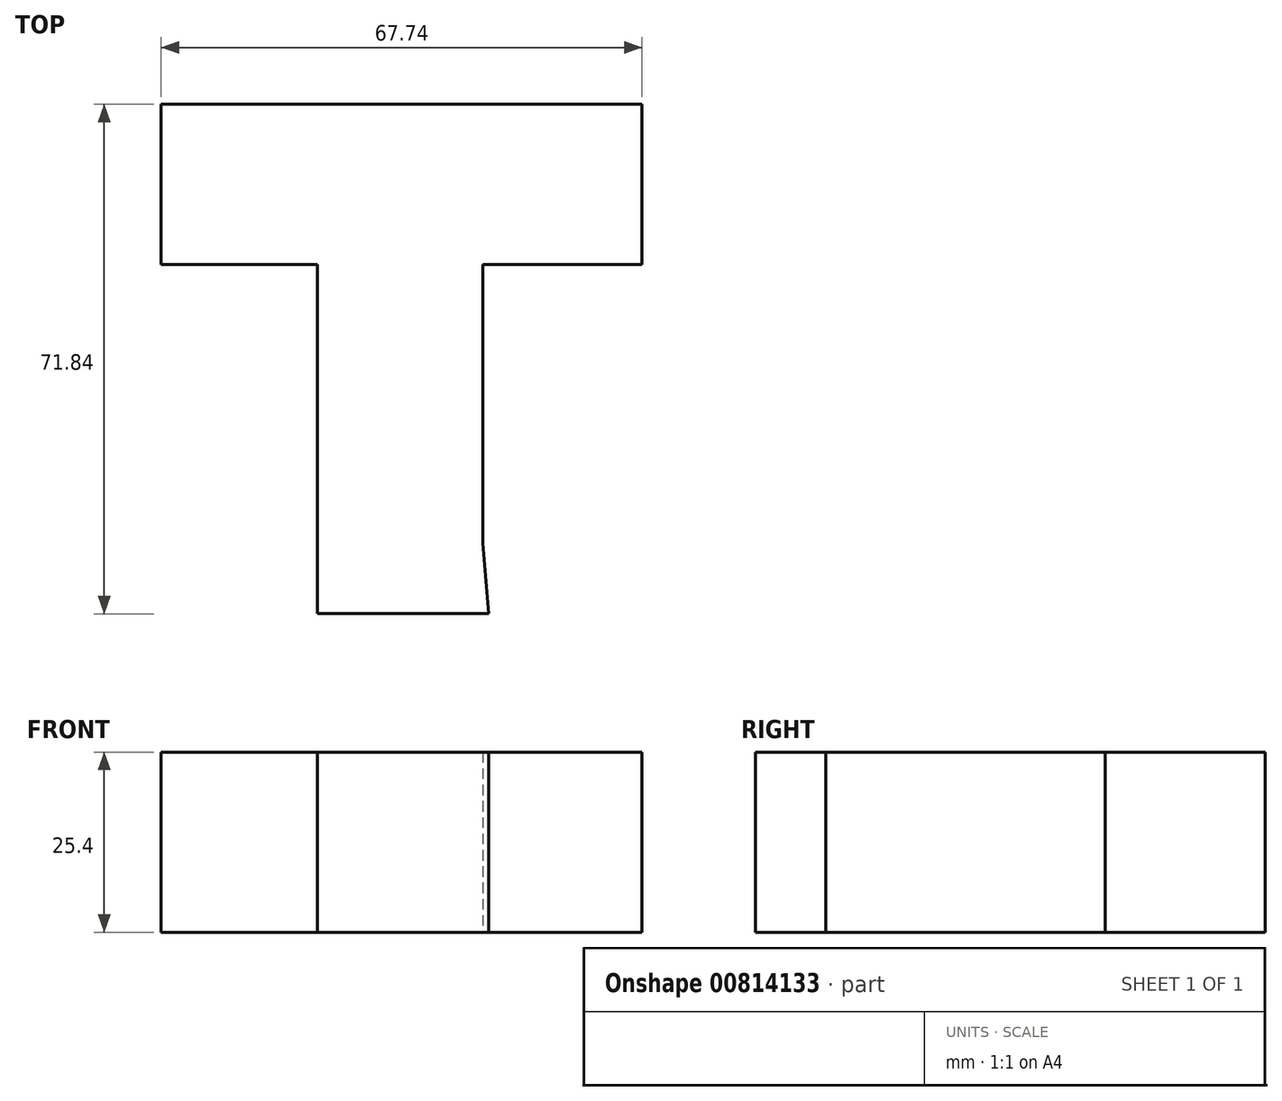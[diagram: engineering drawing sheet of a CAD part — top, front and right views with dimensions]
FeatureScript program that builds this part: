
annotation { "Feature Type Name" : "Feature", "Feature Type Description" : "" }
export const myFeature = defineFeature(function(context is Context, id is Id, definition is map)
    precondition{}
    {
        {
            var Q0;
            Q0=qCreatedBy(makeId("Top.planeOp"),FACE);
            var sketch = newSketch(context, id + "F0", { "sketchPlane" : qUnion([Q0])});
            skLineSegment(sketch, "E0.bottom", {"start": v(-34.16, 58.89) * mm, "end": v(33.58, 58.89) * mm});
            skLineSegment(sketch, "E0.top", {"start": v(-34.16, 36.3) * mm, "end": v(33.58, 36.3) * mm});
            skLineSegment(sketch, "E0.left", {"start": v(-34.16, 58.89) * mm, "end": v(-34.16, 36.3) * mm});
            skLineSegment(sketch, "E0.right", {"start": v(33.58, 58.89) * mm, "end": v(33.58, 36.3) * mm});
            skLineSegment(sketch, "E1", {"start": v(-12.17, 36.3) * mm, "end": v(-12.17, -12.95) * mm});
            skLineSegment(sketch, "E2", {"start": v(11.2, 36.3) * mm, "end": v(11.2, -11.97) * mm});
            skLineSegment(sketch, "E3", {"start": v(-12.17, -12.95) * mm, "end": v(11.97, -12.95) * mm});
            skLineSegment(sketch, "E4", {"start": v(11.97, -12.95) * mm, "end": v(11.2, -3.02) * mm});
            skSolve(sketch);
        }
        {
            var Q0;
            Q0=makeQuery(id+"F0.imprint","IMPRINT",FACE,{"disambiguationData":[TD([[makeQuery(id+"F0.imprint","IMPRINT",EDGE,{"derivedFrom":sQuery(id+"F0.wireOp",EDGE,"E0.bottom")}),-1.0]])]});
            var Q1;
            {var subQ0=sQuery(id+"F0.wireOp",EDGE,"E1");Q1=makeQuery(id+"F0.imprint","IMPRINT",FACE,{"disambiguationData":[TD([[makeQuery(id+"F0.imprint","IMPRINT",EDGE,{"derivedFrom":subQ0}),1.0]])]});}
            extrude(context, id + "F1", {"entities" : qUnion([Q0, Q1]), "depth" : 25.4 * mm, "offsetDistance" : 25.4 * mm});
        }
    });
